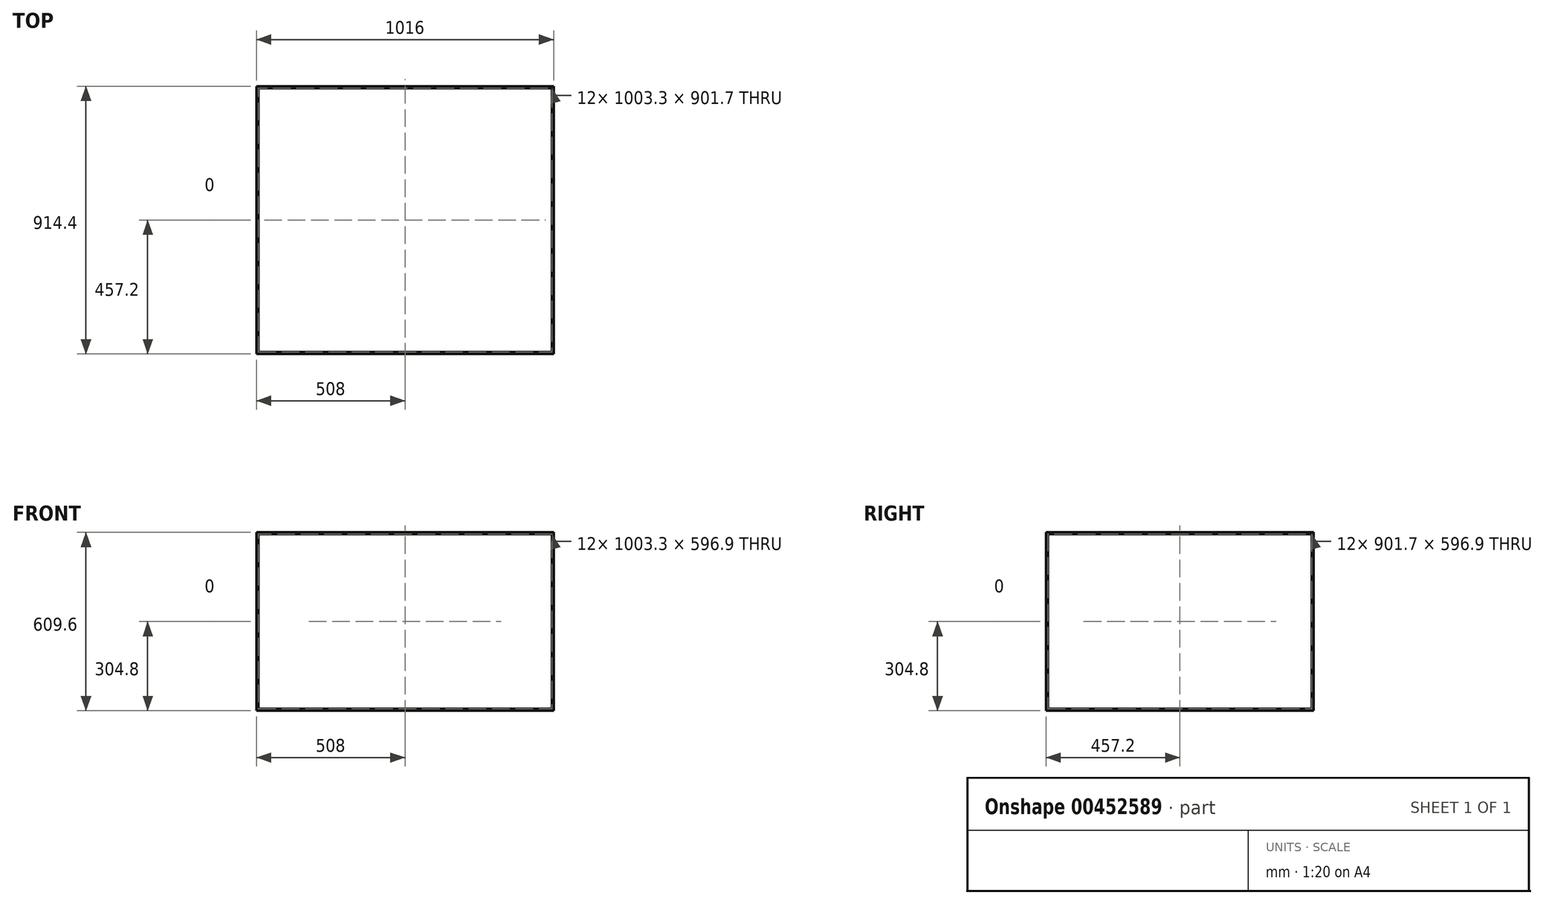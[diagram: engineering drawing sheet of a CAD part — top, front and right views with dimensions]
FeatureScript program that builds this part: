
annotation { "Feature Type Name" : "Feature", "Feature Type Description" : "" }
export const myFeature = defineFeature(function(context is Context, id is Id, definition is map)
    precondition{}
    {
        {
            var Q0;
            Q0=qCreatedBy(makeId("Top.planeOp"),FACE);
            var sketch = newSketch(context, id + "F0", { "sketchPlane" : qUnion([Q0])});
            skLineSegment(sketch, "E0.bottom", {"start": v(508, 457.2) * mm, "end": v(-508, 457.2) * mm});
            skLineSegment(sketch, "E0.top", {"start": v(508, -457.2) * mm, "end": v(-508, -457.2) * mm});
            skLineSegment(sketch, "E0.left", {"start": v(508, 457.2) * mm, "end": v(508, -457.2) * mm});
            skLineSegment(sketch, "E0.right", {"start": v(-508, 457.2) * mm, "end": v(-508, -457.2) * mm});
            skPoint(sketch, "E0.middle", {"position": v(0, 0) * mm});
            skSolve(sketch);
        }
        {
            var Q0;
            Q0=qSketchRegion(id+"F0",true);
            extrude(context, id + "F1", {"entities" : qUnion([Q0]), "depth" : 609.6 * mm});
        }
        {
            var Q0;
            Q0=makeQuery(id+"F1.opExtrude","CAP_FACE",FACE,{"disambiguationData":[OSD([sQuery(id+"F0.wireOp",EDGE,"E0.bottom"),sQuery(id+"F0.wireOp",EDGE,"E0.top"),sQuery(id+"F0.wireOp",EDGE,"E0.left"),sQuery(id+"F0.wireOp",EDGE,"E0.right")])],"isStart":false});
            var sketch = newSketch(context, id + "F2", { "sketchPlane" : qUnion([Q0])});
            skLineSegment(sketch, "E1.bottom", {"start": v(501.65, 450.85) * mm, "end": v(-501.65, 450.85) * mm});
            skLineSegment(sketch, "E1.top", {"start": v(501.65, -450.85) * mm, "end": v(-501.65, -450.85) * mm});
            skLineSegment(sketch, "E1.left", {"start": v(501.65, 450.85) * mm, "end": v(501.65, -450.85) * mm});
            skLineSegment(sketch, "E1.right", {"start": v(-501.65, 450.85) * mm, "end": v(-501.65, -450.85) * mm});
            skPoint(sketch, "E1.middle", {"position": v(0, 0) * mm});
            skSolve(sketch);
        }
        {
            var Q0;
            Q0=qSketchRegion(id+"F2",true);
            extrude(context, id + "F3", {"entities" : qUnion([Q0]), "operationType" : NewBodyOperationType.REMOVE, "endBound" : BoundingType.THROUGH_ALL, "oppositeDirection" : true, "depth" : 25.4 * mm});
        }
        {
            var Q0;
            Q0=makeQuery(id+"F1.opExtrude","SWEPT_FACE",FACE,{"disambiguationData":[OSD([sQuery(id+"F0.wireOp",EDGE,"E0.left")])]});
            var sketch = newSketch(context, id + "F4", { "sketchPlane" : qUnion([Q0])});
            skLineSegment(sketch, "E2.bottom", {"start": v(450.85, 603.25) * mm, "end": v(-450.85, 603.25) * mm});
            skLineSegment(sketch, "E2.top", {"start": v(450.85, 6.35) * mm, "end": v(-450.85, 6.35) * mm});
            skLineSegment(sketch, "E2.left", {"start": v(450.85, 603.25) * mm, "end": v(450.85, 6.35) * mm});
            skLineSegment(sketch, "E2.right", {"start": v(-450.85, 603.25) * mm, "end": v(-450.85, 6.35) * mm});
            skPoint(sketch, "E2.middle", {"position": v(0, 304.8) * mm});
            skPoint(sketch, "E2.middle.positionSnap0", {"position": v(457.2, 304.8) * mm});
            skPoint(sketch, "E2.middle.positionSnap1", {"position": v(0, 609.6) * mm});
            skPoint(sketch, "E2.centerSnap0", {"position": v(457.2, 304.8) * mm});
            skPoint(sketch, "E2.centerSnap1", {"position": v(0, 609.6) * mm});
            skSolve(sketch);
        }
        {
            var Q0;
            Q0=qSketchRegion(id+"F4",true);
            extrude(context, id + "F5", {"entities" : qUnion([Q0]), "operationType" : NewBodyOperationType.REMOVE, "endBound" : BoundingType.THROUGH_ALL, "oppositeDirection" : true, "depth" : 25.4 * mm});
        }
        {
            var Q0;
            Q0=makeQuery(id+"F1.opExtrude","SWEPT_FACE",FACE,{"disambiguationData":[OSD([sQuery(id+"F0.wireOp",EDGE,"E0.bottom")])]});
            var sketch = newSketch(context, id + "F6", { "sketchPlane" : qUnion([Q0])});
            skLineSegment(sketch, "E3.bottom", {"start": v(501.65, 603.25) * mm, "end": v(-501.65, 603.25) * mm});
            skLineSegment(sketch, "E3.top", {"start": v(501.65, 6.35) * mm, "end": v(-501.65, 6.35) * mm});
            skLineSegment(sketch, "E3.left", {"start": v(501.65, 603.25) * mm, "end": v(501.65, 6.35) * mm});
            skLineSegment(sketch, "E3.right", {"start": v(-501.65, 603.25) * mm, "end": v(-501.65, 6.35) * mm});
            skPoint(sketch, "E3.middle", {"position": v(0, 304.8) * mm});
            skPoint(sketch, "E3.middle.positionSnap0", {"position": v(508, 304.8) * mm});
            skPoint(sketch, "E3.centerSnap0", {"position": v(508, 304.8) * mm});
            skSolve(sketch);
        }
        {
            var Q0;
            Q0=qSketchRegion(id+"F6",true);
            extrude(context, id + "F7", {"entities" : qUnion([Q0]), "operationType" : NewBodyOperationType.REMOVE, "endBound" : BoundingType.THROUGH_ALL, "oppositeDirection" : true, "depth" : 25.4 * mm});
        }
    });
